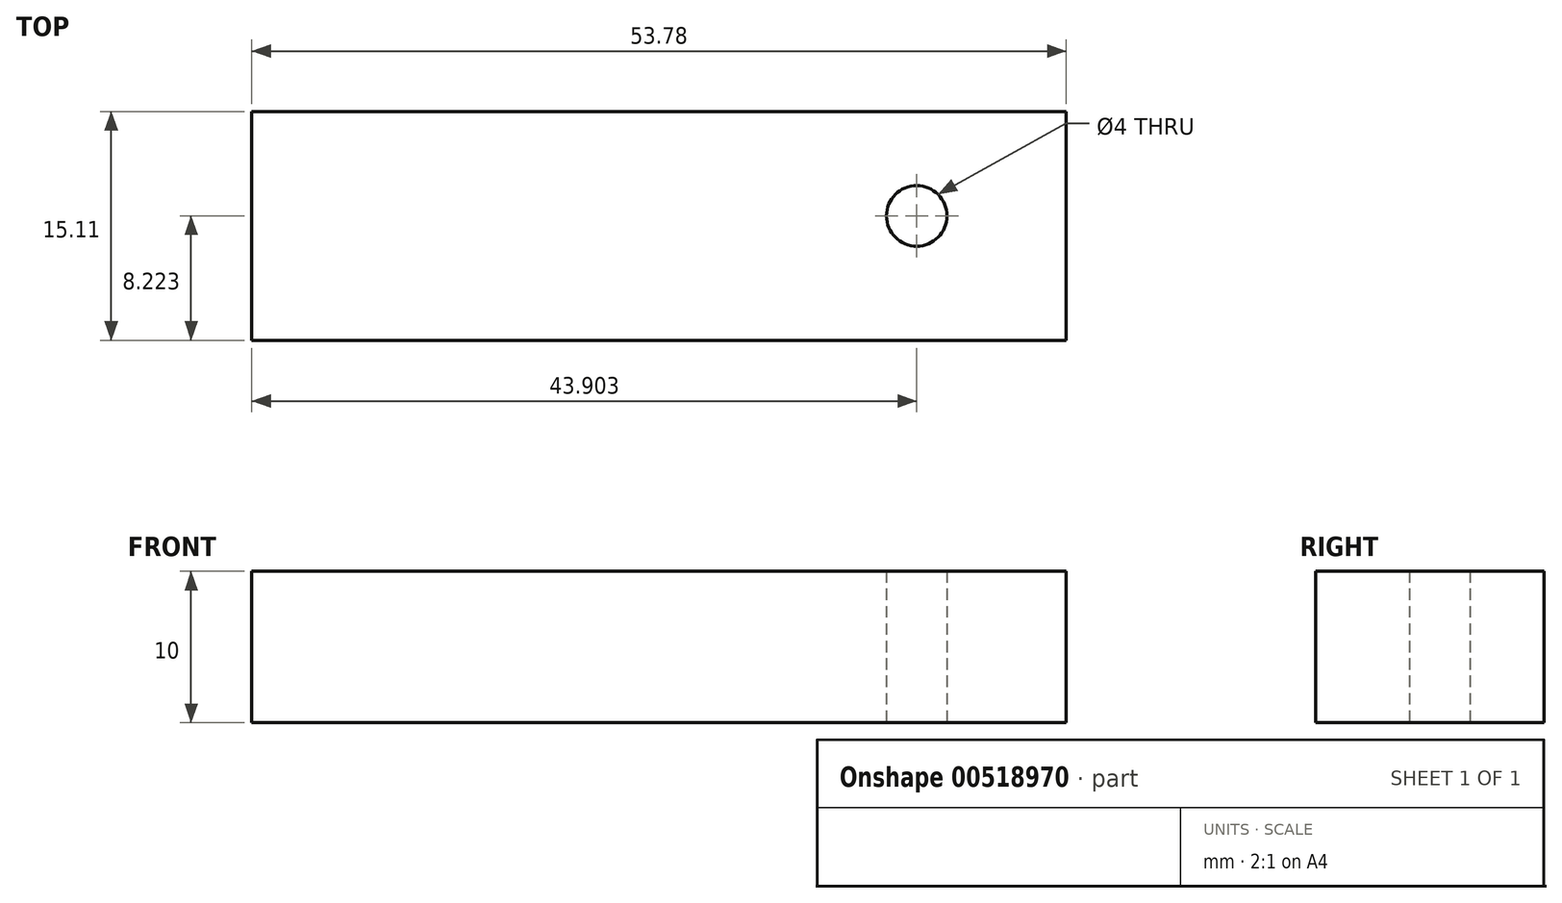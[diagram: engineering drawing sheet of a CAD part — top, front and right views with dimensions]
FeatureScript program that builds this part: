
annotation { "Feature Type Name" : "Feature", "Feature Type Description" : "" }
export const myFeature = defineFeature(function(context is Context, id is Id, definition is map)
    precondition{}
    {
        {
            var Q0;
            Q0=qCreatedBy(makeId("Top.planeOp"),FACE);
            var sketch = newSketch(context, id + "F0", { "sketchPlane" : qUnion([Q0])});
            skLineSegment(sketch, "E0.bottom", {"start": v(-25.38, 22.71) * mm, "end": v(28.4, 22.71) * mm});
            skLineSegment(sketch, "E0.top", {"start": v(-25.38, 7.6) * mm, "end": v(28.4, 7.6) * mm});
            skLineSegment(sketch, "E0.left", {"start": v(-25.38, 22.71) * mm, "end": v(-25.38, 7.6) * mm});
            skLineSegment(sketch, "E0.right", {"start": v(28.4, 22.71) * mm, "end": v(28.4, 7.6) * mm});
            skCircle(sketch, "E1", {"center": v(18.52, 15.82) * mm, "radius": 2 * mm});
            skSolve(sketch);
        }
        {
            var Q0;
            Q0=makeQuery(id+"F0.imprint","IMPRINT",FACE,{"disambiguationData":[TD([[makeQuery(id+"F0.imprint","IMPRINT",EDGE,{"derivedFrom":sQuery(id+"F0.wireOp",EDGE,"E0.bottom")}),-1.0]])]});
            extrude(context, id + "F1", {"entities" : qUnion([Q0]), "depth" : 10 * mm, "offsetDistance" : 25 * mm});
        }
    });
